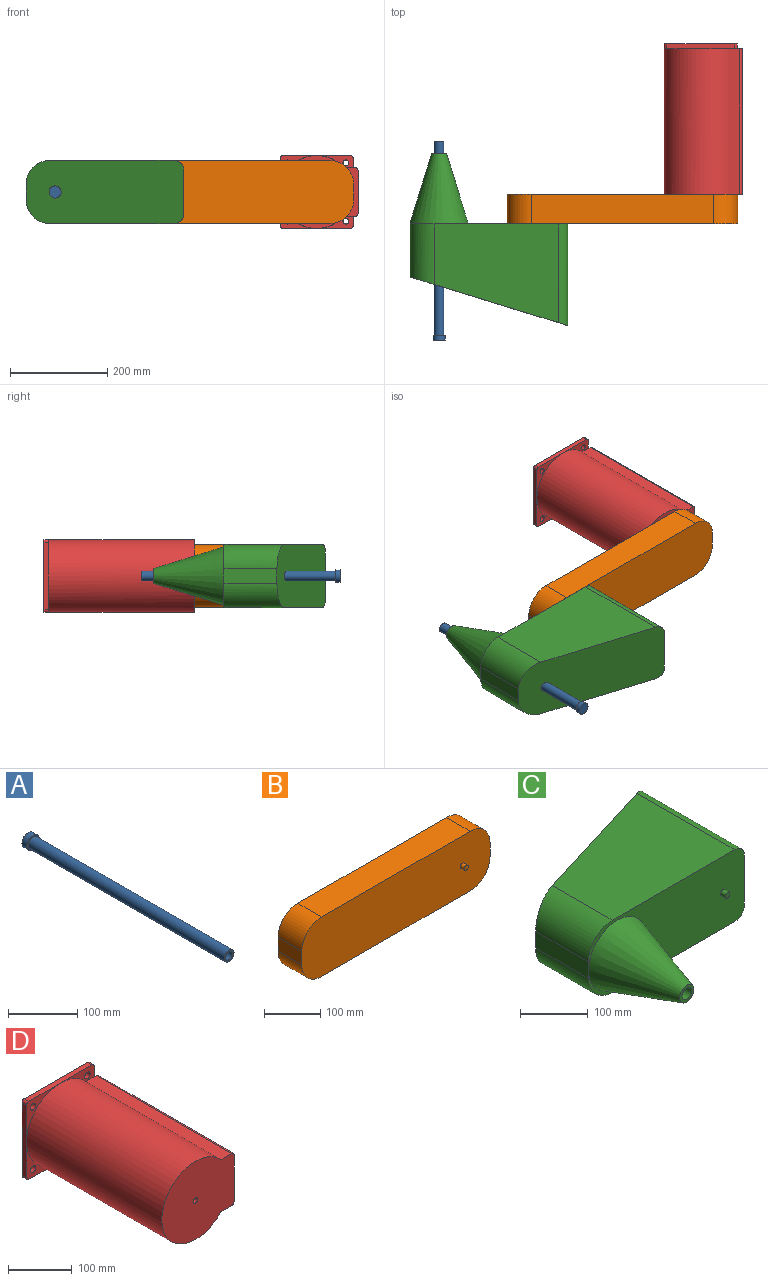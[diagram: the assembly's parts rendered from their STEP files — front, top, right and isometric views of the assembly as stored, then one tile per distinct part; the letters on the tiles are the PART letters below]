
ASSEMBLY  parts=4 mates=4
PART A: 7 faces, bbox 25x410x25 mm
  f0: cylinder r=7mm len=400mm, axis (0,1,0), area 17592.9mm2, adj f2,f6
  f1: cylinder r=10mm len=400mm, axis (0,1,0), area 25132.7mm2, adj f2,f3
  f2: plane 20x20mm, normal (0,-1,0), area 160.2mm2, adj f0,f1
  f3: plane 25x25mm, normal (0,-1,0), area 176.7mm2, adj f1,f5
  f4: plane 25x25mm, normal (0,1,0), area 490.9mm2, adj f5
  f5: cylinder r=12.5mm len=25mm, axis (0,-1,0), area 785.4mm2, adj f3,f4
  f6: plane 14x14mm, normal (0,-1,0), area 153.9mm2, adj f0
PART B: 14 faces, bbox 475x70x130 mm
  f0: plane 375x60mm, normal (0,0,1), area 22500mm2, adj f4,f5,f10,f13
  f1: plane 60x30mm, normal (-1,0,0), area 1800mm2, adj f4,f5,f10,f11
  f2: plane 375x60mm, normal (0,0,-1), area 22500mm2, adj f4,f5,f11,f12
  f3: plane 60x30mm, normal (1,0,0), area 1800mm2, adj f4,f5,f12,f13
  f4: plane 475x130mm, normal (0,-1,0), area 59525.4mm2, adj f0,f1,f2,f3,f6,f10,f11,f12
  f5: plane 475x130mm, normal (0,1,0), area 59525.4mm2, adj f0,f1,f2,f3,f8,f10,f11,f12
  f6: cylinder r=5mm len=10mm, axis (0,1,0), area 314.2mm2, adj f4,f7
  f7: plane 10x10mm, normal (0,-1,0), area 78.5mm2, adj f6
  f8: cylinder r=5mm len=10mm, axis (0,1,0), area 314.2mm2, adj f5,f9
  f9: plane 10x10mm, normal (0,1,0), area 78.5mm2, adj f8
  f10: cylinder r=50mm len=60mm, axis (0,-1,0), area 4712.4mm2, adj f0,f1,f4,f5
  f11: cylinder r=50mm len=60mm, axis (0,1,0), area 4712.4mm2, adj f1,f2,f4,f5
  f12: cylinder r=50mm len=60mm, axis (0,-1,0), area 4712.4mm2, adj f2,f3,f4,f5
  f13: cylinder r=50mm len=60mm, axis (0,1,0), area 4712.4mm2, adj f0,f3,f4,f5
PART C: 15 faces, bbox 326.3x356.3x131.3 mm
  f0: plane 210x90mm, normal (1,0,0), area 18900mm2, adj f1,f7,f8,f11
  f1: cylinder r=20mm len=210mm, axis (0,1,0), area 6527.1mm2, adj f0,f2,f8,f11
  f2: plane 255x203.85mm, normal (0,0,1), area 41976.9mm2, adj f1,f3,f8,f11
  f3: cylinder r=50mm len=125.38mm, axis (0,1,0), area 9078.5mm2, adj f2,f4,f8,f11
  f4: plane 110x30mm, normal (-1,0,0), area 3300mm2, adj f3,f5,f8,f11
  f5: cylinder r=50mm len=125.38mm, axis (0,1,0), area 9078.5mm2, adj f4,f6,f8,f11
  f6: plane 255x203.85mm, normal (0,0,-1), area 41976.9mm2, adj f5,f7,f8,f11
  f7: cylinder r=20mm len=210mm, axis (0,1,0), area 6527.1mm2, adj f0,f6,f8,f11
  f8: plane 325x130mm, normal (0,-1,0), area 29617mm2, adj f0,f1,f2,f3,f4,f5,f6,f7
  f9: cylinder r=5mm len=10mm, axis (0,1,0), area 314.2mm2, adj f8,f10
  f10: plane 10x10mm, normal (0,-1,0), area 78.5mm2, adj f9
  f11: plane 326.29x131.29mm, normal (-0.29,0.96,0), area 42573.8mm2, adj f0,f1,f2,f3,f4,f5,f6,f7
  f12: cone r=15mm half-angle=17.2deg, axis (0,1,0), area 35772.3mm2, adj f8,f13
  f13: plane 30x30mm, normal (0,-1,0), area 392.7mm2, adj f12,f14
  f14: cylinder r=10mm len=276.54mm, axis (0,-1,0), area 17182.1mm2, adj f11,f13
PART D: 27 faces, bbox 160x310x150 mm
  f0: plane 75x25mm, normal (0,-1,0), area 788.6mm2, adj f3,f9,f10,f13,f14,f26
  f1: plane 75x25mm, normal (0,-1,0), area 788.6mm2, adj f5,f8,f10,f14,f15,f25
  f2: plane 75x75mm, normal (0,-1,0), area 1088.7mm2, adj f3,f4,f6,f14,f23
  f3: plane 140x10mm, normal (0,0,1), area 1400mm2, adj f0,f2,f12,f23,f26
  f4: plane 140x10mm, normal (-1,0,0), area 1400mm2, adj f2,f11,f12,f23,f24
  f5: plane 140x10mm, normal (0,0,-1), area 1400mm2, adj f1,f11,f12,f24,f25
  f6: cylinder r=6mm len=12mm, axis (0,1,0), area 377mm2, adj f2,f12
  f7: cylinder r=6mm len=12mm, axis (0,1,0), area 377mm2, adj f11,f12
  f8: cylinder r=6mm len=12mm, axis (0,1,0), area 377mm2, adj f1,f12
  f9: cylinder r=6mm len=12mm, axis (0,1,0), area 377mm2, adj f0,f12
  f10: plane 140x10mm, normal (1,0,0), area 1400mm2, adj f0,f1,f12,f18,f25,f26
  f11: plane 75x75mm, normal (0,-1,0), area 1088.7mm2, adj f4,f5,f7,f14,f24
  f12: plane 150x150mm, normal (0,1,0), area 22026.2mm2, adj f3,f4,f5,f6,f7,f8,f9,f10
  f13: plane 300x24.1mm, normal (0,0,1), area 7229.5mm2, adj f0,f14,f17,f18,f22
  f14: cylinder r=75mm len=300mm, axis (0,1,0), area 108533.9mm2, adj f0,f1,f2,f11,f13,f15,f17
  f15: plane 300x24.1mm, normal (0,0,-1), area 7229.5mm2, adj f1,f14,f17,f18,f21
  f16: plane 300x90mm, normal (1,0,0), area 27000mm2, adj f17,f18,f21,f22
  f17: plane 160x150mm, normal (0,-1,0), area 19182.4mm2, adj f13,f14,f15,f16,f19,f21,f22
  f18: plane 100x10mm, normal (0,1,0), area 989.3mm2, adj f10,f13,f15,f16,f21,f22
  f19: cylinder r=5mm len=10mm, axis (0,-1,0), area 314.2mm2, adj f17,f20
  f20: plane 10x10mm, normal (0,-1,0), area 78.5mm2, adj f19
  f21: cylinder r=5mm len=300mm, axis (0,-1,0), area 2356.2mm2, adj f15,f16,f17,f18
  f22: cylinder r=5mm len=300mm, axis (0,1,0), area 2356.2mm2, adj f13,f16,f17,f18
  f23: cylinder r=5mm len=10mm, axis (0,-1,0), area 78.5mm2, adj f2,f3,f4,f12
  f24: cylinder r=5mm len=10mm, axis (0,1,0), area 78.5mm2, adj f4,f5,f11,f12
  f25: cylinder r=5mm len=10mm, axis (0,-1,0), area 78.5mm2, adj f1,f5,f10,f12
  f26: cylinder r=5mm len=10mm, axis (0,1,0), area 78.5mm2, adj f0,f3,f10,f12
PLACE A rot(axis=(1,0,0),180deg) t=(-387.65,-683.26,128.39)mm
PLACE B rot(axis=(1,0,0),180deg) t=(-172.65,-453.26,118.39)mm
PLACE C rot(axis=(1,0,0),180deg) t=(-285.15,-463.26,128.39)mm
PLACE D t=(151.05,-83.26,128.39)mm fixed
MATE parallel C.f9 <-> B.f8  axis (0,1,0) through (-167.65,-453.26,128.39)mm
MATE parallel A.f1 <-> C.f14  axis (0,-1,0) through (-387.65,-483.26,128.39)mm
MATE parallel B.f6 <-> D.f17  axis (0,1,0) through (157.35,-393.26,128.39)mm
MATE parallel C.f14 <-> A.f1  axis (0,1,0) through (-387.65,-308.26,128.39)mm
